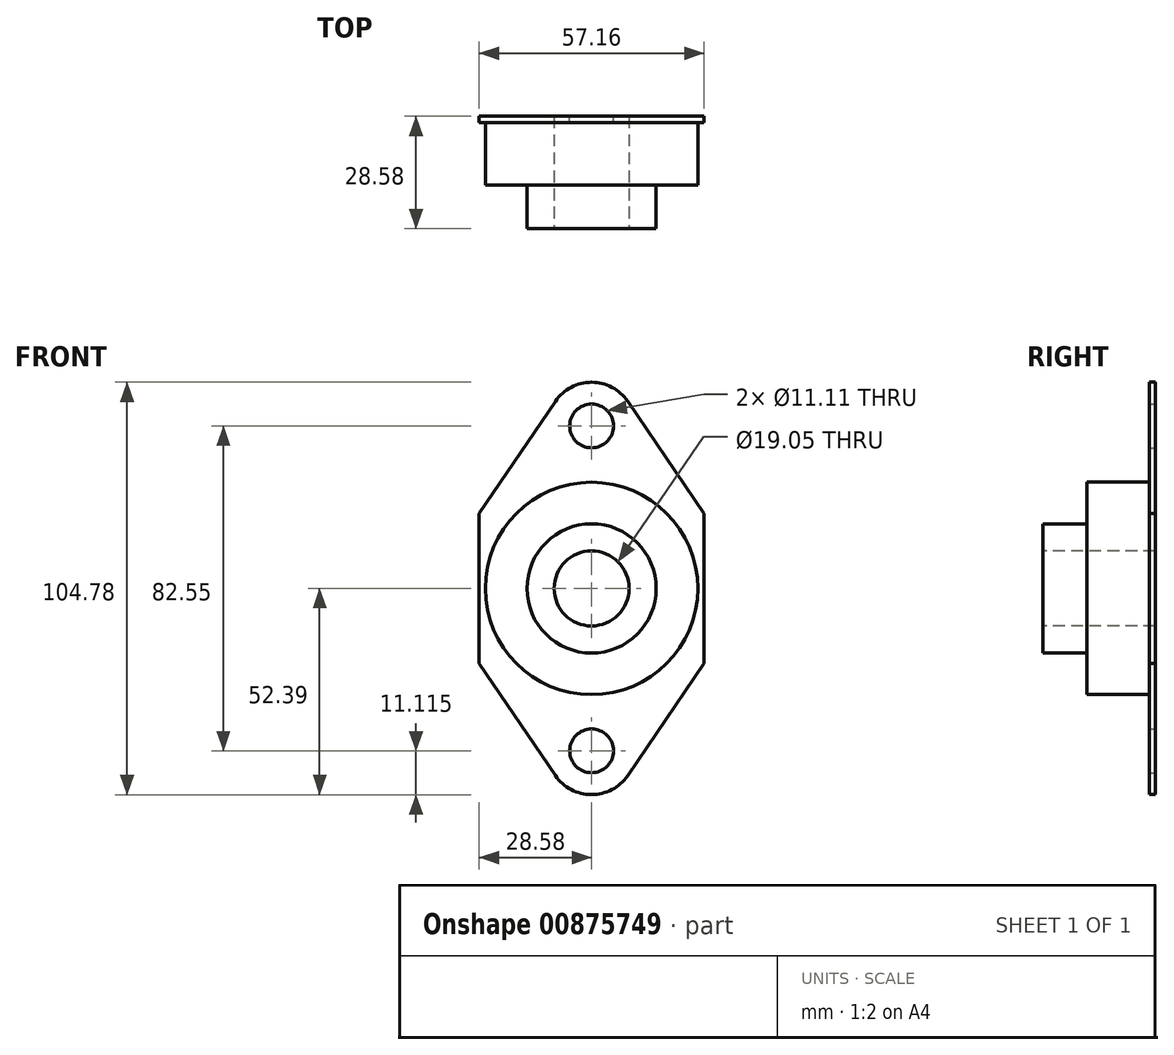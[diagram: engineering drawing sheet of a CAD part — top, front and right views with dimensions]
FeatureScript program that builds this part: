
annotation { "Feature Type Name" : "Feature", "Feature Type Description" : "" }
export const myFeature = defineFeature(function(context is Context, id is Id, definition is map)
    precondition{}
    {
        {
            var Q0;
            Q0=qCreatedBy(makeId("Front.planeOp"),FACE);
            var sketch = newSketch(context, id + "F0", { "sketchPlane" : qUnion([Q0])});
            skCircle(sketch, "E0", {"center": v(0, 41.28) * mm, "radius": 5.56 * mm});
            skCircle(sketch, "E1", {"center": v(0, -41.28) * mm, "radius": 5.56 * mm});
            skArc(sketch, "E2", {"start": v(9.19, 47.53) * mm, "mid": v(0, 52.39) * mm, "end": v(-9.19, 47.53) * mm});
            skArc(sketch, "E3", {"start": v(-9.19, -47.53) * mm, "mid": v(0, -52.39) * mm, "end": v(9.19, -47.53) * mm});
            skLineSegment(sketch, "E4.bottom", {"start": v(28.58, 19.05) * mm, "end": v(-28.58, 19.05) * mm, "construction": true});
            skLineSegment(sketch, "E4.top", {"start": v(28.58, -19.05) * mm, "end": v(-28.58, -19.05) * mm, "construction": true});
            skLineSegment(sketch, "E4.left", {"start": v(28.58, 19.05) * mm, "end": v(28.58, -19.05) * mm});
            skLineSegment(sketch, "E4.right", {"start": v(-28.58, 19.05) * mm, "end": v(-28.58, -19.05) * mm});
            skPoint(sketch, "E4.middle", {"position": v(0, 0) * mm});
            skLineSegment(sketch, "E5", {"start": v(-28.57, -19.05) * mm, "end": v(-9.19, -47.53) * mm});
            skLineSegment(sketch, "E6", {"start": v(-28.58, 19.05) * mm, "end": v(-9.19, 47.53) * mm});
            skLineSegment(sketch, "E7", {"start": v(28.58, 19.05) * mm, "end": v(9.19, 47.53) * mm});
            skLineSegment(sketch, "E8", {"start": v(28.58, -19.05) * mm, "end": v(9.19, -47.53) * mm});
            skSolve(sketch);
        }
        {
            var Q0;
            Q0=makeQuery(id+"F0.imprint","IMPRINT",FACE,{"disambiguationData":[TD([[makeQuery(id+"F0.imprint","IMPRINT",EDGE,{"derivedFrom":sQuery(id+"F0.wireOp",EDGE,"E0")}),-1.0]])]});
            extrude(context, id + "F1", {"entities" : qUnion([Q0]), "depth" : 1.57 * mm, "offsetDistance" : 25.4 * mm});
        }
        {
            var Q0;
            Q0=makeQuery(id+"F1.opExtrude","CAP_FACE",FACE,{"disambiguationData":[OSD([sQuery(id+"F0.wireOp",EDGE,"E0"),sQuery(id+"F0.wireOp",EDGE,"E1"),sQuery(id+"F0.wireOp",EDGE,"E2"),sQuery(id+"F0.wireOp",EDGE,"E3"),sQuery(id+"F0.wireOp",EDGE,"E4.left"),sQuery(id+"F0.wireOp",EDGE,"E4.right"),sQuery(id+"F0.wireOp",EDGE,"E5"),sQuery(id+"F0.wireOp",EDGE,"E6"),sQuery(id+"F0.wireOp",EDGE,"E7"),sQuery(id+"F0.wireOp",EDGE,"E8")])],"isStart":false});
            var sketch = newSketch(context, id + "F2", { "sketchPlane" : qUnion([Q0])});
            skCircle(sketch, "E9", {"center": v(0, 0) * mm, "radius": 26.99 * mm});
            skSolve(sketch);
        }
        {
            var Q0;
            Q0=makeQuery(id+"F2.imprint","IMPRINT",FACE,{"disambiguationData":[TD([[makeQuery(id+"F2.imprint","IMPRINT",EDGE,{"derivedFrom":sQuery(id+"F2.wireOp",EDGE,"E9")}),1.0]])]});
            extrude(context, id + "F3", {"entities" : qUnion([Q0]), "operationType" : NewBodyOperationType.ADD, "depth" : 15.9 * mm, "offsetDistance" : 25.4 * mm});
        }
        {
            var Q0;
            Q0=makeQuery(id+"F3.opExtrude","CAP_FACE",FACE,{"disambiguationData":[OSD([sQuery(id+"F2.wireOp",EDGE,"E9")])],"isStart":false});
            var sketch = newSketch(context, id + "F4", { "sketchPlane" : qUnion([Q0])});
            skCircle(sketch, "E10", {"center": v(0, 0) * mm, "radius": 16.42 * mm});
            skSolve(sketch);
        }
        {
            var Q0;
            Q0=makeQuery(id+"F4.imprint","IMPRINT",FACE,{"disambiguationData":[TD([[makeQuery(id+"F4.imprint","IMPRINT",EDGE,{"derivedFrom":sQuery(id+"F4.wireOp",EDGE,"E10")}),1.0]])]});
            extrude(context, id + "F5", {"entities" : qUnion([Q0]), "operationType" : NewBodyOperationType.ADD, "depth" : 11.1 * mm, "offsetDistance" : 25.4 * mm});
        }
        {
            var Q0;
            Q0=makeQuery(id+"F5.opExtrude","CAP_FACE",FACE,{"disambiguationData":[OSD([sQuery(id+"F4.wireOp",EDGE,"E10")])],"isStart":false});
            var sketch = newSketch(context, id + "F6", { "sketchPlane" : qUnion([Q0])});
            skCircle(sketch, "E11", {"center": v(0, 0) * mm, "radius": 9.53 * mm});
            skSolve(sketch);
        }
        {
            var Q0;
            Q0=makeQuery(id+"F6.imprint","IMPRINT",FACE,{"disambiguationData":[TD([[makeQuery(id+"F6.imprint","IMPRINT",EDGE,{"derivedFrom":sQuery(id+"F6.wireOp",EDGE,"E11")}),1.0]])]});
            extrude(context, id + "F7", {"entities" : qUnion([Q0]), "operationType" : NewBodyOperationType.REMOVE, "endBound" : BoundingType.UP_TO_NEXT, "oppositeDirection" : true, "depth" : 25.4 * mm, "offsetDistance" : 25.4 * mm});
        }
    });
